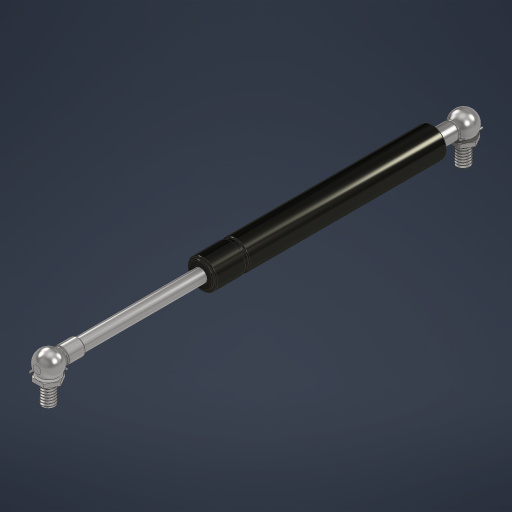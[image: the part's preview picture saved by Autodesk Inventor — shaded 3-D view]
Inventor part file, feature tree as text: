
AUTODESK INVENTOR PART (.ipt)
format: ipt  version: 2024 (Build 280153000, 153)  size: 1,349,632 bytes
history: native  units: in
note: dims shown in document units (in); Inventor stores cm internally (conversion verified against a paired STEP export)
features: other x7, revolve x2, fillet x1, sweep x1, pattern_circular x1
ambient origin geometry x8: Origin, YZ Plane, XZ Plane, XY Plane, X Axis, Y Axis, Z Axis, Center Point
bodies: Solid1 (feature_tree), Solid2 (feature_tree), Solid3 (feature_tree), Solid4 (feature_tree), Solid5 (feature_tree), Solid6 (feature_tree), Solid7 (feature_tree), Solid8 (feature_tree), Solid9 (feature_tree), Solid10 (feature_tree), Solid11 (feature_tree), Solid12 (feature_tree)
feature tree (12):
  fillet  "Fillet1"  [1 undecoded]
  revolve  "Revolve2[1]"  [1 undecoded]
  revolve  "Revolve2[2]"  [1 undecoded]
  sweep  "Sweep3"
  other  "Cut-Extrude2"
  other  "CirPattern2[1]"
  other  "CirPattern2[3]"
  other  "Boss-Extrude2[1]"
  other  "Split1[3]"
  other  "Split1[4]"
  pattern_circular  "CirPattern6"
  other  "Boss-Extrude2[2]"
note: 3 required parameter values undecoded (feature->parameter linkage not recoverable at this tier; creation-order binding heuristic only, values carry confidence <= 0.55)
